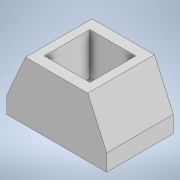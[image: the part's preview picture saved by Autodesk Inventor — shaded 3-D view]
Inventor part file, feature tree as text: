
AUTODESK INVENTOR PART (.ipt)
format: ipt  version: 2022 (Build 260153000, 153)  size: 126,976 bytes
history: native  units: mm
features: extrude x4, sketch x4
ambient origin geometry x8: Origin, YZ Plane, XZ Plane, XY Plane, X Axis, Y Axis, Z Axis, Center Point
bodies: Solid1 (feature_tree)
feature tree (8):
  extrude  "Extrusion1"  Depth=40.0mm
  extrude  "Extrusion2"  Depth=35.4mm
  extrude  "Extrusion3"  Depth=25.4mm
  extrude  "Extrusion4"  TaperAngle=0.0deg  [1 undecoded]
  sketch  "Sketch1"  dims[d0=60.0mm d1=40.0mm]
  sketch  "Sketch2"  dims[d2=35.4mm d3=0.0mm d9=5.0mm]
  sketch  "Sketch3"  dims[d10=25.4mm d11=0.0mm d12=18.7mm]
  sketch  "Sketch4"  dims[d13=10.0mm d14=0.0mm d15=0.0mm d20=3.0mm d21=10.0mm d22=0.0mm]
note: 1 required parameter value undecoded (feature->parameter linkage not recoverable at this tier; creation-order binding heuristic only, values carry confidence <= 0.55)
